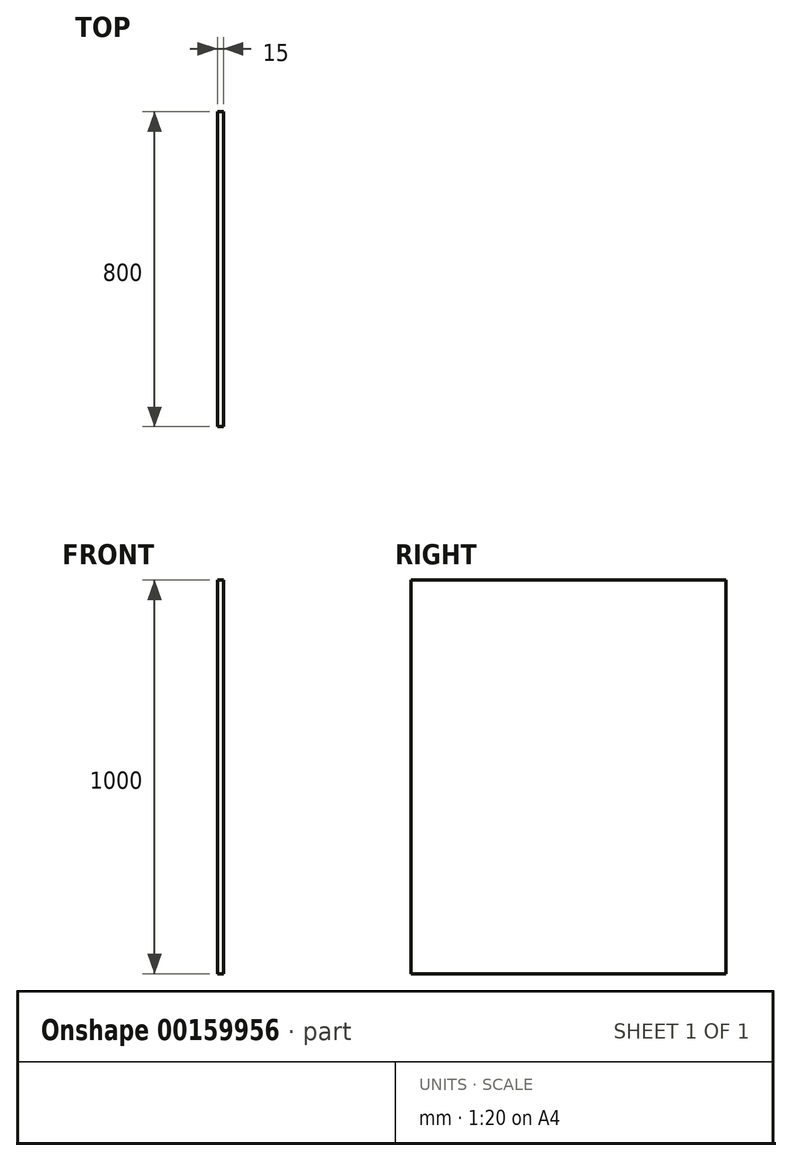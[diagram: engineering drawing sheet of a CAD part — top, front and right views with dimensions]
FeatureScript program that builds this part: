
annotation { "Feature Type Name" : "Feature", "Feature Type Description" : "" }
export const myFeature = defineFeature(function(context is Context, id is Id, definition is map)
    precondition{}
    {
        {
            var Q0;
            Q0=qCreatedBy(makeId("Right.planeOp"),FACE);
            var sketch = newSketch(context, id + "F0", { "sketchPlane" : qUnion([Q0])});
            skLineSegment(sketch, "E0.bottom", {"start": v(-36.61, 925.17) * mm, "end": v(763.39, 925.17) * mm});
            skLineSegment(sketch, "E0.top", {"start": v(-36.61, -74.83) * mm, "end": v(763.39, -74.83) * mm});
            skLineSegment(sketch, "E0.left", {"start": v(-36.61, 925.17) * mm, "end": v(-36.61, -74.83) * mm});
            skLineSegment(sketch, "E0.right", {"start": v(763.39, 925.17) * mm, "end": v(763.39, -74.83) * mm});
            skSolve(sketch);
        }
        {
            var Q0;
            Q0=makeQuery(id+"F0.imprint","IMPRINT",FACE,{"disambiguationData":[TD([[makeQuery(id+"F0.imprint","IMPRINT",EDGE,{"derivedFrom":sQuery(id+"F0.wireOp",EDGE,"E0.bottom")}),-1.0]])]});
            extrude(context, id + "F1", {"entities" : qUnion([Q0]), "depth" : 15 * mm});
        }
    });
